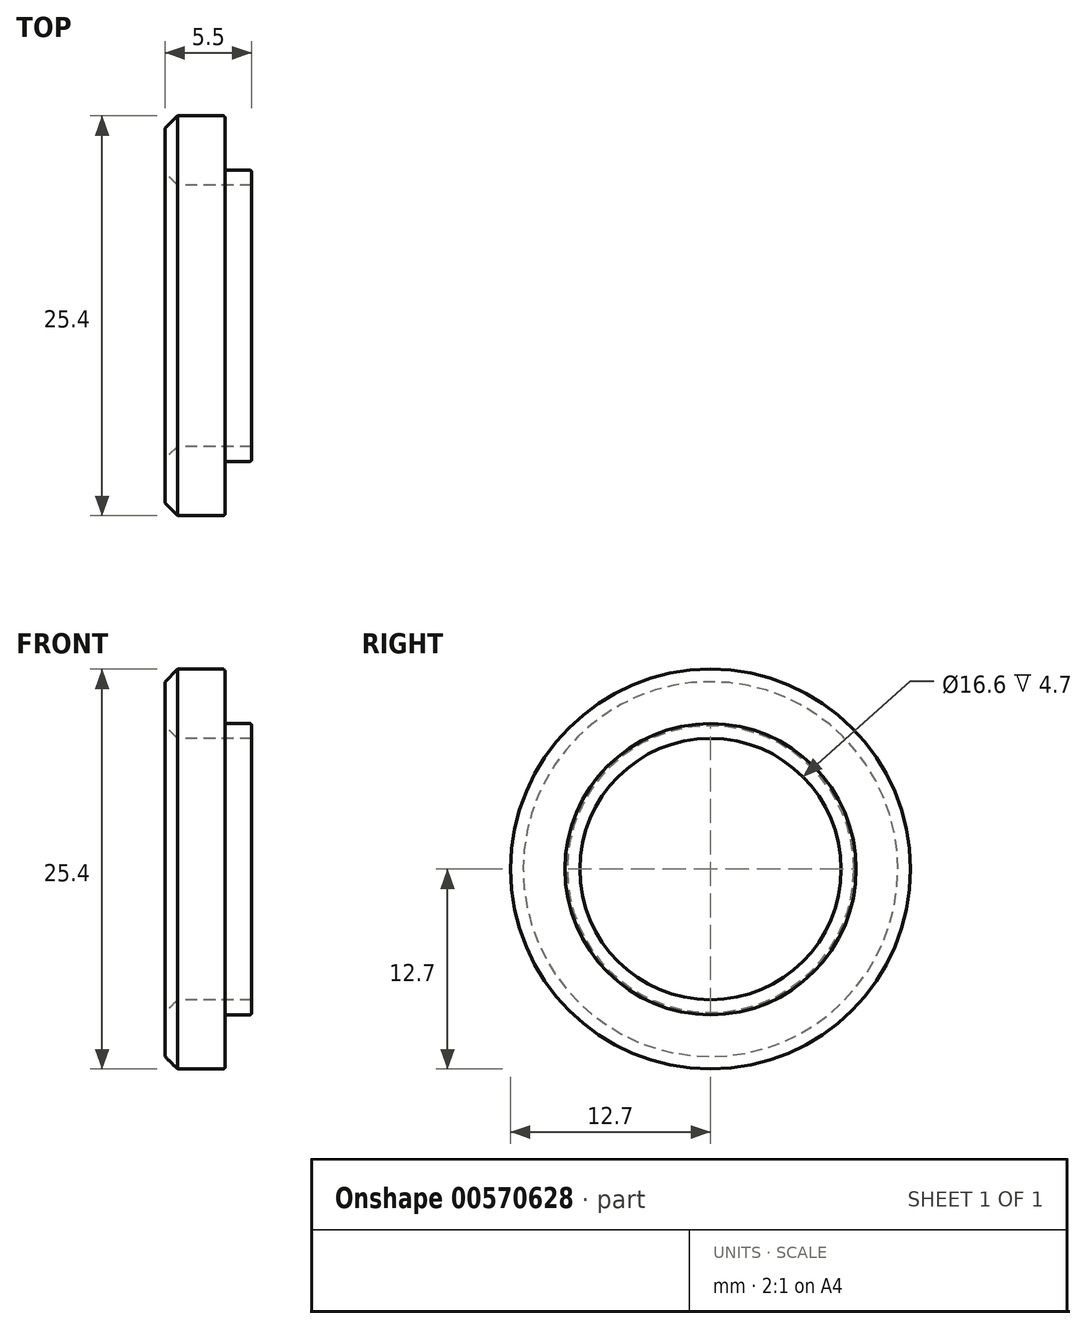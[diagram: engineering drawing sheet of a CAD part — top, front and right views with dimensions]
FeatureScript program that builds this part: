
annotation { "Feature Type Name" : "Feature", "Feature Type Description" : "" }
export const myFeature = defineFeature(function(context is Context, id is Id, definition is map)
    precondition{}
    {
        {
            var Q0;
            Q0=qCreatedBy(makeId("Top.planeOp"),FACE);
            var sketch = newSketch(context, id + "F0", { "sketchPlane" : qUnion([Q0])});
            skLineSegment(sketch, "E0", {"start": v(-28.88, 0) * mm, "end": v(-9.88, 0) * mm, "construction": true});
            skLineSegment(sketch, "E1", {"start": v(-19.8, 12.7) * mm, "end": v(-19.8, 8.3) * mm});
            skLineSegment(sketch, "E2", {"start": v(-19.8, 8.3) * mm, "end": v(-14.3, 8.3) * mm});
            skLineSegment(sketch, "E3", {"start": v(-14.3, 8.3) * mm, "end": v(-14.3, 9.25) * mm});
            skLineSegment(sketch, "E4", {"start": v(-14.3, 9.25) * mm, "end": v(-16, 9.25) * mm});
            skLineSegment(sketch, "E5", {"start": v(-16, 9.25) * mm, "end": v(-16, 12.7) * mm});
            skLineSegment(sketch, "E6", {"start": v(-16, 12.7) * mm, "end": v(-19.8, 12.7) * mm});
            skLineSegment(sketch, "E7.filletArc", {"start": v(-19.8, 12.7) * mm, "end": v(-19.8, 12.7) * mm});
            skLineSegment(sketch, "E8.MirrorCS", {"start": v(-14.3, -9.25) * mm, "end": v(-16, -9.25) * mm});
            skLineSegment(sketch, "E9.MirrorCS", {"start": v(-16, -9.25) * mm, "end": v(-16, -12.7) * mm});
            skLineSegment(sketch, "E10.MirrorCS", {"start": v(-16, -12.7) * mm, "end": v(-19.8, -12.7) * mm});
            skLineSegment(sketch, "E11.MirrorCS", {"start": v(-19.8, -12.7) * mm, "end": v(-19.8, -8.3) * mm});
            skLineSegment(sketch, "E12.MirrorCS", {"start": v(-19.8, -8.3) * mm, "end": v(-14.3, -8.3) * mm});
            skLineSegment(sketch, "E13.MirrorCS", {"start": v(-14.3, -8.3) * mm, "end": v(-14.3, -9.25) * mm});
            skSolve(sketch);
        }
        {
            var Q0;
            Q0=makeQuery(id+"F0.imprint","IMPRINT",FACE,{"disambiguationData":[TD([[makeQuery(id+"F0.imprint","IMPRINT",EDGE,{"derivedFrom":sQuery(id+"F0.wireOp",EDGE,"E1")}),1.0]])]});
            var Q1;
            Q1=sQuery(id+"F0.wireOp",EDGE,"E0");
            revolve(context, id + "F1", {"entities" : qUnion([Q0]), "axis" : qUnion([Q1]), "revolveType" : RevolveType.FULL});
        }
        {
            var Q0;
            Q0=makeQuery(id+"F1.opRevolve","SWEPT_EDGE",EDGE,{"disambiguationData":[OSD([sQuery(id+"F0.wireOp",EDGE,"E1"),sQuery(id+"F0.wireOp",EDGE,"E2")])]});
            var Q1;
            Q1=makeQuery(id+"F1.opRevolve","SWEPT_EDGE",EDGE,{"disambiguationData":[OSD([sQuery(id+"F0.wireOp",EDGE,"E1"),sQuery(id+"F0.wireOp",EDGE,"E6")])]});
            chamfer(context, id + "F2", {"entities" : qUnion([Q0, Q1]), "width" : 0.8 * mm, "tangentPropagation" : true});
        }
        {
            var Q0;
            Q0=makeQuery(id+"F1.opRevolve","SWEPT_EDGE",EDGE,{"disambiguationData":[OSD([sQuery(id+"F0.wireOp",EDGE,"E4"),sQuery(id+"F0.wireOp",EDGE,"E5")])]});
            var Q1;
            Q1=makeQuery(id+"F1.opRevolve","SWEPT_EDGE",EDGE,{"disambiguationData":[OSD([sQuery(id+"F0.wireOp",EDGE,"E3"),sQuery(id+"F0.wireOp",EDGE,"E4")])]});
            var Q2;
            Q2=makeQuery(id+"F1.opRevolve","SWEPT_EDGE",EDGE,{"disambiguationData":[OSD([sQuery(id+"F0.wireOp",EDGE,"E5"),sQuery(id+"F0.wireOp",EDGE,"E6")])]});
            fillet(context, id + "F3", {"entities" : qUnion([Q0, Q1, Q2]), "radius" : 0.12 * mm, "tangentPropagation" : true, "allowEdgeOverflow" : false});
        }
    });
